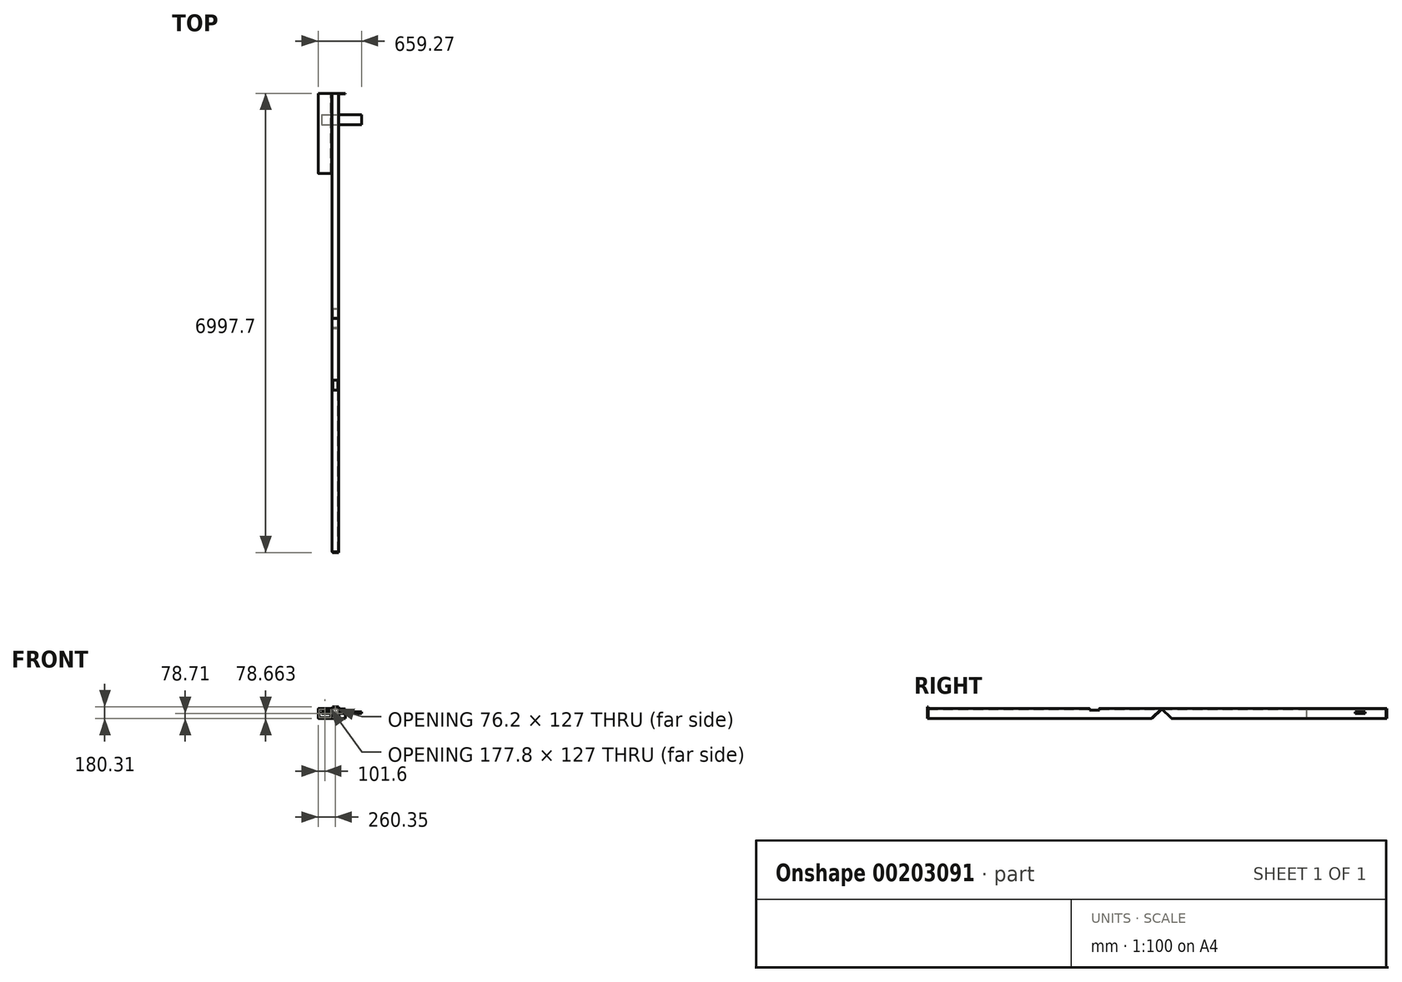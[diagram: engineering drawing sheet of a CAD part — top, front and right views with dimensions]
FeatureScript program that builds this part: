
annotation { "Feature Type Name" : "Feature", "Feature Type Description" : "" }
export const myFeature = defineFeature(function(context is Context, id is Id, definition is map)
    precondition{}
    {
        {
            var Q0;
            Q0=qCreatedBy(makeId("Front.planeOp"),FACE);
            var sketch = newSketch(context, id + "F0", { "sketchPlane" : qUnion([Q0])});
            skLineSegment(sketch, "E0.bottom", {"start": v(50.8, -76.2) * mm, "end": v(-50.8, -76.2) * mm});
            skLineSegment(sketch, "E0.top", {"start": v(50.8, 76.2) * mm, "end": v(-50.8, 76.2) * mm});
            skLineSegment(sketch, "E0.left", {"start": v(50.8, -76.2) * mm, "end": v(50.8, 76.2) * mm});
            skLineSegment(sketch, "E0.right", {"start": v(-50.8, -76.2) * mm, "end": v(-50.8, 76.2) * mm});
            skPoint(sketch, "E0.middle", {"position": v(0, 0) * mm});
            skLineSegment(sketch, "E1.0", {"start": v(38.1, 63.5) * mm, "end": v(-38.1, 63.5) * mm});
            skLineSegment(sketch, "E1.1", {"start": v(38.1, -63.5) * mm, "end": v(38.1, 63.5) * mm});
            skLineSegment(sketch, "E1.2", {"start": v(38.1, -63.5) * mm, "end": v(-38.1, -63.5) * mm});
            skLineSegment(sketch, "E1.3", {"start": v(-38.1, -63.5) * mm, "end": v(-38.1, 63.5) * mm});
            skSolve(sketch);
        }
        {
            var Q0;
            Q0=qCreatedBy(makeId("Front.planeOp"),FACE);
            var sketch = newSketch(context, id + "F1", { "sketchPlane" : qUnion([Q0])});
            skLineSegment(sketch, "E2.bottom", {"start": v(-57.15, -76.25) * mm, "end": v(-260.35, -76.25) * mm});
            skLineSegment(sketch, "E2.top", {"start": v(-57.15, 76.15) * mm, "end": v(-260.35, 76.15) * mm});
            skLineSegment(sketch, "E2.left", {"start": v(-57.15, -76.25) * mm, "end": v(-57.15, 76.15) * mm});
            skLineSegment(sketch, "E2.right", {"start": v(-260.35, -76.25) * mm, "end": v(-260.35, 76.15) * mm});
            skLineSegment(sketch, "E3.0", {"start": v(-247.65, -63.55) * mm, "end": v(-247.65, 63.45) * mm});
            skLineSegment(sketch, "E3.1", {"start": v(-69.85, -63.55) * mm, "end": v(-247.65, -63.55) * mm});
            skLineSegment(sketch, "E3.2", {"start": v(-69.85, -63.55) * mm, "end": v(-69.85, 63.45) * mm});
            skLineSegment(sketch, "E3.3", {"start": v(-69.85, 63.45) * mm, "end": v(-247.65, 63.45) * mm});
            skSolve(sketch);
        }
        {
            var Q0;
            Q0=qCreatedBy(makeId("Front.planeOp"),FACE);
            var sketch = newSketch(context, id + "F2", { "sketchPlane" : qUnion([Q0])});
            skLineSegment(sketch, "E4.bottom", {"start": v(59.44, 69.57) * mm, "end": v(154.69, 69.57) * mm});
            skLineSegment(sketch, "E4.top", {"start": v(59.44, -76.48) * mm, "end": v(154.69, -76.48) * mm});
            skLineSegment(sketch, "E4.left", {"start": v(59.44, 69.57) * mm, "end": v(59.44, -76.48) * mm});
            skLineSegment(sketch, "E4.right", {"start": v(154.69, 69.57) * mm, "end": v(154.69, -76.48) * mm});
            skSolve(sketch);
        }
        {
            var Q0;
            Q0=makeQuery(id+"F1.imprint","IMPRINT",FACE,{"disambiguationData":[TD([[makeQuery(id+"F1.imprint","IMPRINT",EDGE,{"derivedFrom":sQuery(id+"F1.wireOp",EDGE,"E2.bottom")}),-1.0]])]});
            extrude(context, id + "F3", {"entities" : qUnion([Q0]), "depth" : 1219.2 * mm});
        }
        {
            var Q0;
            Q0=makeQuery(id+"F0.imprint","IMPRINT",FACE,{"disambiguationData":[TD([[makeQuery(id+"F0.imprint","IMPRINT",EDGE,{"derivedFrom":sQuery(id+"F0.wireOp",EDGE,"E0.bottom")}),-1.0]])]});
            extrude(context, id + "F4", {"entities" : qUnion([Q0]), "depth" : 3429 * mm});
        }
        {
            var Q0;
            Q0=makeQuery(id+"F2.imprint","IMPRINT",FACE,{"disambiguationData":[TD([[makeQuery(id+"F2.imprint","IMPRINT",EDGE,{"derivedFrom":sQuery(id+"F2.wireOp",EDGE,"E4.bottom")}),-1.0]])]});
            extrude(context, id + "F5", {"entities" : qUnion([Q0]), "depth" : 9.52 * mm});
        }
        {
            var Q0;
            Q0=makeQuery(id+"F4.opExtrude","CAP_FACE",FACE,{"disambiguationData":[OSD([sQuery(id+"F0.wireOp",EDGE,"E0.bottom"),sQuery(id+"F0.wireOp",EDGE,"E0.top"),sQuery(id+"F0.wireOp",EDGE,"E0.left"),sQuery(id+"F0.wireOp",EDGE,"E0.right"),sQuery(id+"F0.wireOp",EDGE,"E1.0"),sQuery(id+"F0.wireOp",EDGE,"E1.1"),sQuery(id+"F0.wireOp",EDGE,"E1.2"),sQuery(id+"F0.wireOp",EDGE,"E1.3")])],"isStart":false});
            extrude(context, id + "F6", {"entities" : qUnion([Q0]), "depth" : 3556 * mm});
        }
        {
            var Q0;
            Q0=makeQuery(id+"F6.opExtrude","SWEPT_FACE",FACE,{"disambiguationData":[OSD([sQuery(id+"F0.wireOp",EDGE,"E0.left")])]});
            var sketch = newSketch(context, id + "F7", { "sketchPlane" : qUnion([Q0])});
            skLineSegment(sketch, "E5", {"start": v(-3429, 76.2) * mm, "end": v(-3581.4, -76.2) * mm});
            skSolve(sketch);
        }
        {
            var Q0;
            Q0=makeQuery(id+"F4.opExtrude","SWEPT_FACE",FACE,{"disambiguationData":[OSD([sQuery(id+"F0.wireOp",EDGE,"E0.left")])]});
            var sketch = newSketch(context, id + "F8", { "sketchPlane" : qUnion([Q0])});
            skLineSegment(sketch, "E6", {"start": v(-3429, 76.2) * mm, "end": v(-3276.6, -76.2) * mm});
            skSolve(sketch);
        }
        {
            var Q0;
            Q0 = qSketchRegion(id + "F8", true);
            var Q1;
            {var subQ0=sQuery(id+"F8.wireOp",EDGE,"E6");Q1=makeQuery(id+"F8.imprint","IMPRINT",FACE,{"disambiguationData":[TD([[makeQuery(id+"F8.imprint","IMPRINT",EDGE,{"derivedFrom":subQ0}),-1.0]])]});}
            extrude(context, id + "F9", {"entities" : qUnion([Q0, Q1]), "operationType" : NewBodyOperationType.REMOVE, "endBound" : BoundingType.THROUGH_ALL, "oppositeDirection" : true, "depth" : 25.4 * mm});
        }
        {
            var Q0;
            {var subQ0=sQuery(id+"F7.wireOp",EDGE,"E5");Q0=makeQuery(id+"F7.imprint","IMPRINT",FACE,{"disambiguationData":[TD([[makeQuery(id+"F7.imprint","IMPRINT",EDGE,{"derivedFrom":subQ0}),1.0]])]});}
            extrude(context, id + "F10", {"entities" : qUnion([Q0]), "operationType" : NewBodyOperationType.REMOVE, "endBound" : BoundingType.THROUGH_ALL, "oppositeDirection" : true, "depth" : 25.4 * mm});
        }
        {
            var Q0;
            Q0=makeQuery(id+"F10.boolean.opBoolean","COPY",FACE,{"derivedFrom":makeQuery(id+"F10.opExtrude","SWEPT_FACE",FACE,{"disambiguationData":[OSD([sQuery(id+"F7.wireOp",EDGE,"E5")])]})});
            var sketch = newSketch(context, id + "F11", { "sketchPlane" : qUnion([Q0])});
            skLineSegment(sketch, "E7", {"start": v(-44.45, -2580.34) * mm, "end": v(-44.45, -2370.79) * mm});
            skLineSegment(sketch, "E8", {"start": v(-44.45, -2370.79) * mm, "end": v(50.8, -2370.79) * mm});
            skLineSegment(sketch, "E9", {"start": v(50.8, -2370.79) * mm, "end": v(50.8, -2580.34) * mm});
            skLineSegment(sketch, "E10", {"start": v(50.8, -2580.34) * mm, "end": v(-44.45, -2580.34) * mm});
            skSolve(sketch);
        }
        {
            var Q0;
            Q0=makeQuery(id+"F11.imprint","IMPRINT",FACE,{"disambiguationData":[TD([[makeQuery(id+"F11.imprint","IMPRINT",EDGE,{"derivedFrom":sQuery(id+"F11.wireOp",EDGE,"E7")}),-1.0]])]});
            var Q1;
            {var subQ0=makeQuery(id+"F10.opExtrude","SWEPT_FACE",FACE,{"disambiguationData":[OSD([sQuery(id+"F7.wireOp",EDGE,"E5")])]});Q1=makeQuery(id+"F11.imprint","IMPRINT",FACE,{"disambiguationData":[TD([[makeQuery(id+"F11.imprint","IMPRINT",EDGE,{"derivedFrom":makeQuery(id+"F10.boolean.opBoolean","INTERSECT",EDGE,{"derivedFrom":[makeQuery(id+"F6.opExtrude","SWEPT_FACE",FACE,{"disambiguationData":[OSD([sQuery(id+"F0.wireOp",EDGE,"E1.0")])]}),subQ0]})}),-1.0]])]});}
            extrude(context, id + "F12", {"entities" : qUnion([Q0, Q1]), "depth" : 9.52 * mm});
        }
        {
            var Q0;
            Q0=makeQuery(id+"F6.opExtrude","CAP_FACE",FACE,{"disambiguationData":[OSD([sQuery(id+"F0.wireOp",EDGE,"E0.bottom"),sQuery(id+"F0.wireOp",EDGE,"E0.top"),sQuery(id+"F0.wireOp",EDGE,"E0.left"),sQuery(id+"F0.wireOp",EDGE,"E0.right"),sQuery(id+"F0.wireOp",EDGE,"E1.0"),sQuery(id+"F0.wireOp",EDGE,"E1.1"),sQuery(id+"F0.wireOp",EDGE,"E1.2"),sQuery(id+"F0.wireOp",EDGE,"E1.3")])],"isStart":false});
            var sketch = newSketch(context, id + "F13", { "sketchPlane" : qUnion([Q0])});
            skLineSegment(sketch, "E11.bottom", {"start": v(50.8, -76.2) * mm, "end": v(-44.45, -76.2) * mm});
            skLineSegment(sketch, "E11.left", {"start": v(50.8, -76.2) * mm, "end": v(50.8, 101.6) * mm});
            skLineSegment(sketch, "E11.right", {"start": v(-44.45, -76.2) * mm, "end": v(-44.45, 101.6) * mm});
            skPoint(sketch, "E11.middle", {"position": v(0, 0) * mm});
            skLineSegment(sketch, "E12", {"start": v(-44.45, 101.6) * mm, "end": v(50.8, 101.6) * mm});
            skSolve(sketch);
        }
        {
            var Q0;
            {var subQ2=sQuery(id+"F13.wireOp",EDGE,"E11.bottom");Q0=makeQuery(id+"F13.imprint","IMPRINT",FACE,{"disambiguationData":[TD([[makeQuery(id+"F13.imprint","IMPRINT",EDGE,{"derivedFrom":subQ2}),-1.0]])]});}
            var Q1;
            Q1=makeQuery(id+"F13.imprint","IMPRINT",FACE,{"disambiguationData":[TD([[makeQuery(id+"F13.imprint","IMPRINT",EDGE,{"derivedFrom":makeQuery(id+"F6.opExtrude","CAP_EDGE",EDGE,{"disambiguationData":[OSD([sQuery(id+"F0.wireOp",EDGE,"E1.0")])],"isStart":false})}),1.0]])]});
            var Q2;
            {var subQ2=sQuery(id+"F13.wireOp",EDGE,"E12");Q2=makeQuery(id+"F13.imprint","IMPRINT",FACE,{"disambiguationData":[TD([[makeQuery(id+"F13.imprint","IMPRINT",EDGE,{"derivedFrom":subQ2}),-1.0]])]});}
            extrude(context, id + "F14", {"entities" : qUnion([Q0, Q1, Q2]), "depth" : 12.7 * mm});
        }
        {
            var Q0;
            Q0=makeQuery(id+"F4.opExtrude","SWEPT_EDGE",EDGE,{"disambiguationData":[OSD([sQuery(id+"F0.wireOp",EDGE,"E0.top"),sQuery(id+"F0.wireOp",EDGE,"E0.right")])]});
            var Q1;
            Q1=makeQuery(id+"F4.opExtrude","SWEPT_EDGE",EDGE,{"disambiguationData":[OSD([sQuery(id+"F0.wireOp",EDGE,"E0.bottom"),sQuery(id+"F0.wireOp",EDGE,"E0.right")])]});
            var Q2;
            Q2=makeQuery(id+"F4.opExtrude","SWEPT_EDGE",EDGE,{"disambiguationData":[OSD([sQuery(id+"F0.wireOp",EDGE,"E0.bottom"),sQuery(id+"F0.wireOp",EDGE,"E0.left")])]});
            var Q3;
            Q3=makeQuery(id+"F4.opExtrude","SWEPT_EDGE",EDGE,{"disambiguationData":[OSD([sQuery(id+"F0.wireOp",EDGE,"E0.top"),sQuery(id+"F0.wireOp",EDGE,"E0.left")])]});
            var Q4;
            Q4=makeQuery(id+"F4.opExtrude","SWEPT_EDGE",EDGE,{"disambiguationData":[OSD([sQuery(id+"F0.wireOp",EDGE,"E1.0"),sQuery(id+"F0.wireOp",EDGE,"E1.3")])]});
            var Q5;
            Q5=makeQuery(id+"F4.opExtrude","SWEPT_EDGE",EDGE,{"disambiguationData":[OSD([sQuery(id+"F0.wireOp",EDGE,"E1.0"),sQuery(id+"F0.wireOp",EDGE,"E1.1")])]});
            var Q6;
            Q6=makeQuery(id+"F4.opExtrude","SWEPT_EDGE",EDGE,{"disambiguationData":[OSD([sQuery(id+"F0.wireOp",EDGE,"E1.1"),sQuery(id+"F0.wireOp",EDGE,"E1.2")])]});
            var Q7;
            Q7=makeQuery(id+"F4.opExtrude","SWEPT_EDGE",EDGE,{"disambiguationData":[OSD([sQuery(id+"F0.wireOp",EDGE,"E1.2"),sQuery(id+"F0.wireOp",EDGE,"E1.3")])]});
            var Q8;
            Q8=makeQuery(id+"F6.opExtrude","SWEPT_EDGE",EDGE,{"disambiguationData":[OSD([sQuery(id+"F0.wireOp",EDGE,"E0.bottom"),sQuery(id+"F0.wireOp",EDGE,"E0.left")])]});
            var Q9;
            Q9=makeQuery(id+"F6.opExtrude","SWEPT_EDGE",EDGE,{"disambiguationData":[OSD([sQuery(id+"F0.wireOp",EDGE,"E0.bottom"),sQuery(id+"F0.wireOp",EDGE,"E0.right")])]});
            var Q10;
            Q10=makeQuery(id+"F6.opExtrude","SWEPT_EDGE",EDGE,{"disambiguationData":[OSD([sQuery(id+"F0.wireOp",EDGE,"E0.top"),sQuery(id+"F0.wireOp",EDGE,"E0.left")])]});
            var Q11;
            Q11=makeQuery(id+"F6.opExtrude","SWEPT_EDGE",EDGE,{"disambiguationData":[OSD([sQuery(id+"F0.wireOp",EDGE,"E0.top"),sQuery(id+"F0.wireOp",EDGE,"E0.right")])]});
            var Q12;
            Q12=makeQuery(id+"F6.opExtrude","SWEPT_EDGE",EDGE,{"disambiguationData":[OSD([sQuery(id+"F0.wireOp",EDGE,"E1.0"),sQuery(id+"F0.wireOp",EDGE,"E1.3")])]});
            var Q13;
            Q13=makeQuery(id+"F6.opExtrude","SWEPT_EDGE",EDGE,{"disambiguationData":[OSD([sQuery(id+"F0.wireOp",EDGE,"E1.0"),sQuery(id+"F0.wireOp",EDGE,"E1.1")])]});
            var Q14;
            Q14=makeQuery(id+"F6.opExtrude","SWEPT_EDGE",EDGE,{"disambiguationData":[OSD([sQuery(id+"F0.wireOp",EDGE,"E1.1"),sQuery(id+"F0.wireOp",EDGE,"E1.2")])]});
            var Q15;
            Q15=makeQuery(id+"F6.opExtrude","SWEPT_EDGE",EDGE,{"disambiguationData":[OSD([sQuery(id+"F0.wireOp",EDGE,"E1.2"),sQuery(id+"F0.wireOp",EDGE,"E1.3")])]});
            var Q16;
            Q16=makeQuery(id+"F3.opExtrude","SWEPT_EDGE",EDGE,{"disambiguationData":[OSD([sQuery(id+"F1.wireOp",EDGE,"E3.2"),sQuery(id+"F1.wireOp",EDGE,"E3.3")])]});
            var Q17;
            Q17=makeQuery(id+"F3.opExtrude","SWEPT_EDGE",EDGE,{"disambiguationData":[OSD([sQuery(id+"F1.wireOp",EDGE,"E3.1"),sQuery(id+"F1.wireOp",EDGE,"E3.2")])]});
            var Q18;
            Q18=makeQuery(id+"F3.opExtrude","SWEPT_EDGE",EDGE,{"disambiguationData":[OSD([sQuery(id+"F1.wireOp",EDGE,"E3.0"),sQuery(id+"F1.wireOp",EDGE,"E3.1")])]});
            var Q19;
            Q19=makeQuery(id+"F3.opExtrude","SWEPT_EDGE",EDGE,{"disambiguationData":[OSD([sQuery(id+"F1.wireOp",EDGE,"E3.0"),sQuery(id+"F1.wireOp",EDGE,"E3.3")])]});
            var Q20;
            Q20=makeQuery(id+"F3.opExtrude","SWEPT_EDGE",EDGE,{"disambiguationData":[OSD([sQuery(id+"F1.wireOp",EDGE,"E2.bottom"),sQuery(id+"F1.wireOp",EDGE,"E2.left")])]});
            var Q21;
            Q21=makeQuery(id+"F3.opExtrude","SWEPT_EDGE",EDGE,{"disambiguationData":[OSD([sQuery(id+"F1.wireOp",EDGE,"E2.bottom"),sQuery(id+"F1.wireOp",EDGE,"E2.right")])]});
            var Q22;
            Q22=makeQuery(id+"F3.opExtrude","SWEPT_EDGE",EDGE,{"disambiguationData":[OSD([sQuery(id+"F1.wireOp",EDGE,"E2.top"),sQuery(id+"F1.wireOp",EDGE,"E2.right")])]});
            var Q23;
            Q23=makeQuery(id+"F3.opExtrude","SWEPT_EDGE",EDGE,{"disambiguationData":[OSD([sQuery(id+"F1.wireOp",EDGE,"E2.top"),sQuery(id+"F1.wireOp",EDGE,"E2.left")])]});
            fillet(context, id + "F15", {"entities" : qUnion([Q0, Q1, Q2, Q3, Q4, Q5, Q6, Q7, Q8, Q9, Q10, Q11, Q12, Q13, Q14, Q15, Q16, Q17, Q18, Q19, Q20, Q21, Q22, Q23]), "radius" : 5.08 * mm, "tangentPropagation" : true, "allowEdgeOverflow" : false});
        }
        {
            var Q0;
            Q0=qCreatedBy(makeId("Top.planeOp"),FACE);
            var sketch = newSketch(context, id + "F16", { "sketchPlane" : qUnion([Q0])});
            skLineSegment(sketch, "E13.bottom", {"start": v(-210.68, -326.94) * mm, "end": v(398.92, -326.94) * mm});
            skLineSegment(sketch, "E13.top", {"start": v(-210.68, -479.34) * mm, "end": v(398.92, -479.34) * mm});
            skLineSegment(sketch, "E13.left", {"start": v(-210.68, -326.94) * mm, "end": v(-210.68, -479.34) * mm});
            skLineSegment(sketch, "E13.right", {"start": v(398.92, -326.94) * mm, "end": v(398.92, -479.34) * mm});
            skSolve(sketch);
        }
        {
            var Q0;
            Q0 = qSketchRegion(id + "F16", true);
            extrude(context, id + "F17", {"entities" : qUnion([Q0]), "depth" : 25.4 * mm});
        }
        {
            var Q0;
            Q0=makeQuery(id+"F6.opExtrude","SWEPT_FACE",FACE,{"disambiguationData":[OSD([sQuery(id+"F0.wireOp",EDGE,"E0.top")])]});
            var sketch = newSketch(context, id + "F18", { "sketchPlane" : qUnion([Q0])});
            skLineSegment(sketch, "E14", {"start": v(117.98, -4373.88) * mm, "end": v(-129, -4373.88) * mm});
            skLineSegment(sketch, "E15", {"start": v(117.98, -4373.88) * mm, "end": v(117.98, -4526.28) * mm});
            skLineSegment(sketch, "E16", {"start": v(117.98, -4526.28) * mm, "end": v(-129, -4526.28) * mm});
            skLineSegment(sketch, "E17", {"start": v(-129, -4526.28) * mm, "end": v(-129, -4373.88) * mm});
            skSolve(sketch);
        }
        {
            var Q0;
            Q0 = qSketchRegion(id + "F18", true);
            extrude(context, id + "F19", {"entities" : qUnion([Q0]), "operationType" : NewBodyOperationType.REMOVE, "oppositeDirection" : true, "depth" : 25.4 * mm});
        }
    });
